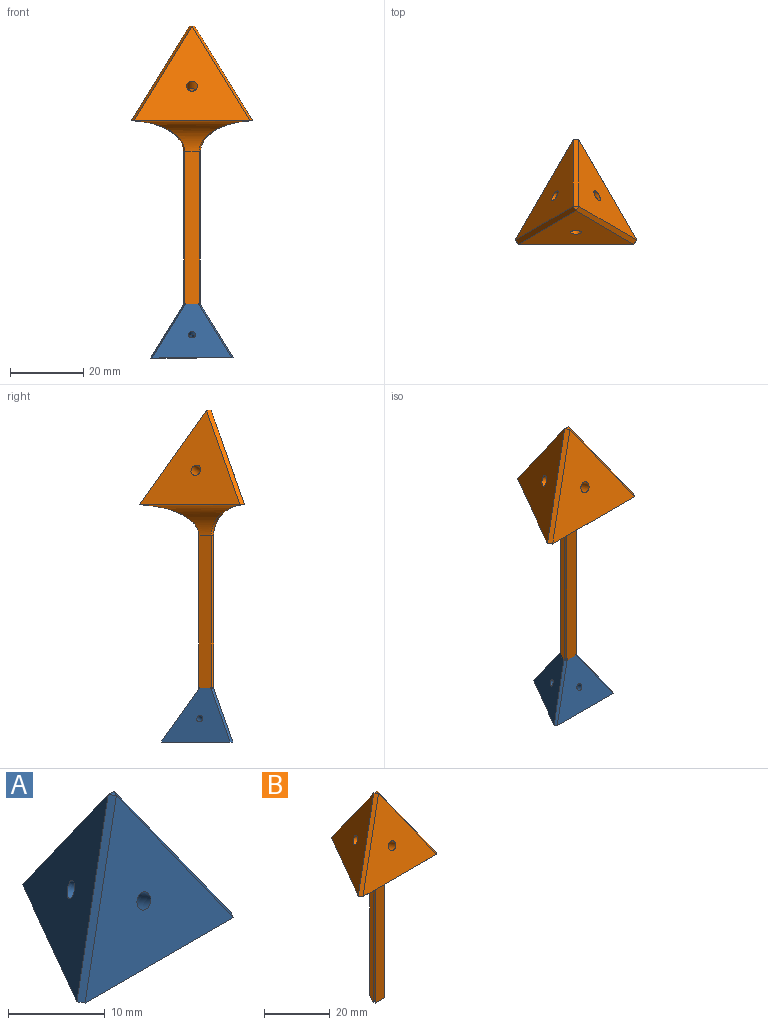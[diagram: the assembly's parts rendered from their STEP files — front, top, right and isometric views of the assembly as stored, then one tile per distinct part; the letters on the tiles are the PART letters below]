
ASSEMBLY  parts=2 mates=1
PART A: 14 faces, bbox 22.6x19.6x17.7 mm
  f0: plane 18.8x17.72mm, normal (-0.82,0.47,0.33), area 201.1mm2, adj f3,f9,f10,f13
  f1: plane 21.7x17.72mm, normal (0,-0.94,0.33), area 201.1mm2, adj f3,f8,f11,f13
  f2: plane 18.8x17.72mm, normal (0.82,0.47,0.33), area 201.1mm2, adj f3,f7,f10,f11
  f3: plane 22.58x19.56mm, normal (0,0,-1), area 150.9mm2, adj f0,f1,f2,f4,f5,f6,f10,f11
  f4: plane 12.24x11.54mm, normal (0.82,-0.47,-0.33), area 83.6mm2, adj f3,f5,f6,f9
  f5: plane 14.13x11.54mm, normal (0,0.94,-0.33), area 83.6mm2, adj f3,f4,f6,f8
  f6: plane 12.24x11.54mm, normal (-0.82,-0.47,-0.33), area 83.6mm2, adj f3,f4,f5,f7
  f7: cylinder r=0.95mm len=3.17mm, axis (0.82,0.47,0.33), area 15.2mm2, adj f2,f6
  f8: cylinder r=0.95mm len=3.03mm, axis (0,-0.94,0.33), area 15.2mm2, adj f1,f5
  f9: cylinder r=0.95mm len=3.17mm, axis (-0.82,0.47,0.33), area 15.2mm2, adj f0,f4
  f10: plane 17.72x12.53mm, normal (0,0.82,0.58), area 19.1mm2, adj f0,f2,f3,f12
  f11: plane 17.72x11.29mm, normal (0.71,-0.41,0.58), area 19.1mm2, adj f1,f2,f3,f12
  f12: plane 0.88x0.76mm, normal (0,0,1), area 0.3mm2, adj f10,f11,f13
  f13: plane 17.72x11.29mm, normal (-0.71,-0.41,0.58), area 19.1mm2, adj f0,f1,f3,f12
PART B: 35 faces, bbox 34.8x33.3x76.7 mm
  f0: plane 3.42x2mm, normal (0,0,-1), area 0.2mm2, adj f20,f25,f29,f34
  f1: plane 3.42x2mm, normal (0,0,-1), area 0.2mm2, adj f19,f27,f29,f32
  f2: plane 27.48x15.87mm, normal (0,0,-1), area 0.3mm2, adj f5,f14,f15,f24
  f3: plane 31.73x0.01mm, normal (0,0,-1), area 0.3mm2, adj f6,f14,f17,f22
  f4: plane 27.48x15.87mm, normal (0,0,-1), area 0.3mm2, adj f7,f15,f17,f23
  f5: plane 27.47x25.9mm, normal (-0.82,0.47,0.33), area 428.6mm2, adj f2,f13,f14,f15
  f6: plane 31.72x25.9mm, normal (0,-0.94,0.33), area 428.6mm2, adj f3,f9,f14,f17
  f7: plane 27.47x25.9mm, normal (0.82,0.47,0.33), area 428.6mm2, adj f4,f11,f15,f17
  f8: cone r=0mm half-angle=59deg, axis (0,-0.94,0.33), area 7mm2, adj f9,f10,f12
  f9: cylinder r=1.5mm len=6.75mm, axis (0,-0.94,0.33), area 57.5mm2, adj f6,f8,f11,f13
  f10: cone r=0mm half-angle=59deg, axis (0.82,0.47,0.33), area 7mm2, adj f8,f11,f12
  f11: cylinder r=1.5mm len=6.71mm, axis (0.82,0.47,0.33), area 57.5mm2, adj f7,f9,f10,f13
  f12: cone r=0mm half-angle=59deg, axis (-0.82,0.47,0.33), area 7mm2, adj f8,f10,f13
  f13: cylinder r=1.5mm len=6.71mm, axis (-0.82,0.47,0.33), area 57.5mm2, adj f5,f9,f11,f12
  f14: plane 25.93x16.6mm, normal (-0.71,-0.41,0.58), area 46.5mm2, adj f2,f3,f5,f6,f16,f22,f24,f28
  f15: plane 25.93x18.34mm, normal (0,0.82,0.58), area 46.5mm2, adj f2,f4,f5,f7,f16,f23,f24,f30
  f16: plane 1.47x1.27mm, normal (0,0,1), area 0.9mm2, adj f14,f15,f17
  f17: plane 25.93x16.6mm, normal (0.71,-0.41,0.58), area 46.5mm2, adj f3,f4,f6,f7,f16,f22,f23,f26
  f18: plane 42.37x3.89mm, normal (0,-1,0), area 164.6mm2, adj f21,f22,f25,f27
  f19: plane 42.37x3.37mm, normal (-0.87,0.5,0), area 164.6mm2, adj f1,f24,f27,f29
  f20: plane 42.37x3.37mm, normal (0.87,0.5,0), area 164.6mm2, adj f0,f23,f25,f29
  f21: plane 3.94x0.05mm, normal (0,0,-1), area 0.2mm2, adj f18,f25,f27,f33
  f22: cylinder r=8.43mm len=32.45mm, axis (1,0,0), area 198.6mm2, adj f3,f14,f17,f18,f26,f28
  f23: cylinder r=8.43mm len=32.32mm, axis (-0.5,0.87,0), area 198.6mm2, adj f4,f15,f17,f20,f26,f30
  f24: cylinder r=8.43mm len=32.32mm, axis (-0.5,-0.87,0), area 198.6mm2, adj f2,f14,f15,f19,f28,f30
  f25: plane 42.37x0.66mm, normal (0.87,-0.5,0), area 32mm2, adj f0,f18,f20,f21,f26,f33,f34
  f26: bspline ~15.44x9.13mm, area 9mm2, adj f17,f22,f23,f25
  f27: plane 42.37x0.66mm, normal (-0.87,-0.5,0), area 32mm2, adj f1,f18,f19,f21,f28,f32,f33
  f28: bspline ~15.44x9.13mm, area 9mm2, adj f14,f22,f24,f27
  f29: plane 42.37x0.76mm, normal (0,1,0), area 32mm2, adj f0,f1,f19,f20,f30,f32,f34
  f30: bspline ~17.6x8.44mm, area 9mm2, adj f15,f23,f24,f29
  f31: plane 0.88x0.76mm, normal (0,0,-1), area 0.3mm2, adj f32,f33,f34
  f32: plane 3.7x3.56mm, normal (0.82,-0.47,-0.33), area 11mm2, adj f1,f27,f29,f31,f33,f34
  f33: plane 4.27x3.56mm, normal (0,0.94,-0.33), area 11mm2, adj f21,f25,f27,f31,f32,f34
  f34: plane 3.7x3.56mm, normal (-0.82,-0.47,-0.33), area 11mm2, adj f0,f25,f29,f31,f32,f33
PLACE A t=(0,0,-64.97)mm
PLACE B at identity
MATE planar A.f12 <-> B.f31  axis (0,0,1) through (0,0,-47.24)mm
